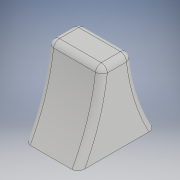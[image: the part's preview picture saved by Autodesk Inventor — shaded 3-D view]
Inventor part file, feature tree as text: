
AUTODESK INVENTOR PART (.ipt)
format: ipt  version: 2018.3 (Build 223284000, 284)  size: 156,160 bytes
history: native  units: mm
features: extrude x3, sketch x3, fillet x1
ambient origin geometry x8: Origin, YZ Plane, XZ Plane, XY Plane, X Axis, Y Axis, Z Axis, Center Point
bodies: Solid1 (feature_tree)
feature tree (7):
  extrude  "Extrusion1"  Depth=13.0mm
  extrude  "Extrusion2"  Depth=4.0mm
  extrude  "Extrusion3"  Depth=1.0mm
  fillet  "Fillet1"  Radius=8.976mm
  sketch  "Sketch1"  dims[d0=13.0mm d1=13.0mm]
  sketch  "Sketch2"  dims[d2=4.0mm d3=4.0mm]
  sketch  "Sketch3"  dims[d4=33.0mm d5=33.0mm d6=8.976mm d7=0.0mm d8=1.5mm d9=5.4mm d10=3.738mm d11=3.9mm d12=2.0mm d13=0.0mm d14=0.0mm d15=0.3mm d16=0.3mm d17=10.0mm d18=0.0mm d19=1.0mm]
